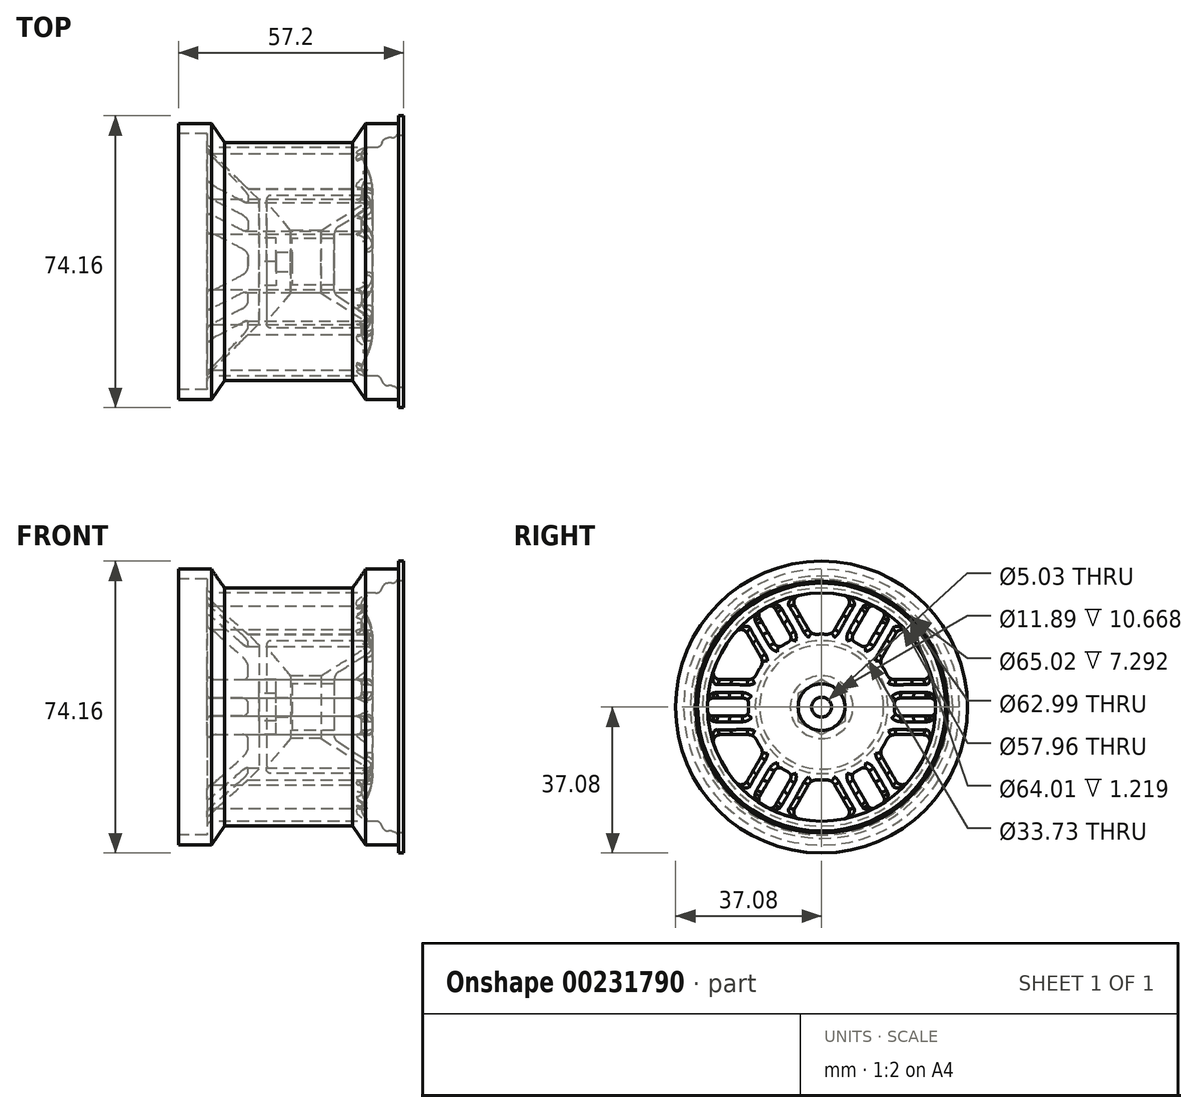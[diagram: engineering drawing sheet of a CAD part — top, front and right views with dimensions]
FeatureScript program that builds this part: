
annotation { "Feature Type Name" : "Feature", "Feature Type Description" : "" }
export const myFeature = defineFeature(function(context is Context, id is Id, definition is map)
    precondition{}
    {
        {
            var Q0;
            Q0=qCreatedBy(makeId("Front.planeOp"),FACE);
            var sketch = newSketch(context, id + "F0", { "sketchPlane" : qUnion([Q0])});
            skLineSegment(sketch, "E0.top", {"start": v(-20.52, 0) * mm, "end": v(36.68, 0) * mm});
            skLineSegment(sketch, "E0.left", {"start": v(-20.52, 35.05) * mm, "end": v(-20.52, 0) * mm});
            skLineSegment(sketch, "E0.right", {"start": v(36.68, 35.05) * mm, "end": v(36.68, 0) * mm});
            skLineSegment(sketch, "E1.top", {"start": v(36.68, 37.08) * mm, "end": v(35.46, 37.08) * mm});
            skLineSegment(sketch, "E1.left", {"start": v(36.68, 35.05) * mm, "end": v(36.68, 37.08) * mm});
            skLineSegment(sketch, "E1.right", {"start": v(35.46, 35.05) * mm, "end": v(35.46, 37.08) * mm});
            skLineSegment(sketch, "E2", {"start": v(35.46, 35.05) * mm, "end": v(36.68, 35.05) * mm, "construction": true});
            skPoint(sketch, "E3", {"position": v(0, 0) * mm});
            skLineSegment(sketch, "E4", {"start": v(-20.52, 35.05) * mm, "end": v(-12.14, 35.05) * mm});
            skLineSegment(sketch, "E5", {"start": v(-12.14, 35.05) * mm, "end": v(-8.76, 30.23) * mm});
            skLineSegment(sketch, "E6", {"start": v(-8.76, 30.23) * mm, "end": v(23.7, 30.23) * mm});
            skLineSegment(sketch, "E7", {"start": v(23.7, 30.23) * mm, "end": v(27.08, 35.05) * mm});
            skLineSegment(sketch, "E8", {"start": v(27.08, 35.05) * mm, "end": v(35.46, 35.05) * mm});
            skLineSegment(sketch, "E9", {"start": v(7.47, 30.23) * mm, "end": v(7.47, 0) * mm, "construction": true});
            skSolve(sketch);
        }
        {
            var Q0;
            Q0=makeQuery(id+"F0.imprint","IMPRINT",FACE,{"disambiguationData":[TD([[makeQuery(id+"F0.imprint","IMPRINT",EDGE,{"derivedFrom":sQuery(id+"F0.wireOp",EDGE,"E0.top")}),1.0]])]});
            var Q1;
            Q1=sQuery(id+"F0.wireOp",EDGE,"E0.top");
            revolve(context, id + "F1", {"entities" : qUnion([Q0]), "axis" : qUnion([Q1]), "revolveType" : RevolveType.FULL});
        }
        {
            var Q0;
            Q0=qCreatedBy(makeId("Right.planeOp"),FACE);
            cPlane(context, id + "F2", {"entities" : qUnion([Q0]), "cplaneType" : CPlaneType.OFFSET, "offset" : 13.2 * mm, "width" : 152.4 * mm, "height" : 152.4 * mm});
        }
        {
            var Q0;
            Q0=qCreatedBy(id+"F2.planeOp",FACE);
            var sketch = newSketch(context, id + "F3", { "sketchPlane" : qUnion([Q0])});
            skPoint(sketch, "E10", {"position": v(0, 0) * mm});
            skSolve(sketch);
        }
        {
            var Q0;
            Q0=sQuery(id+"F3.wireOp",VERTEX,"E10");
            var Q1;
            Q1=makeQuery(id+"F1.opRevolve","SWEPT_BODY",BODY,{"disambiguationData":[OSD([sQuery(id+"F0.wireOp",EDGE,"E0.top"),sQuery(id+"F0.wireOp",EDGE,"E0.left"),sQuery(id+"F0.wireOp",EDGE,"E0.right"),sQuery(id+"F0.wireOp",EDGE,"E1.top"),sQuery(id+"F0.wireOp",EDGE,"E1.left"),sQuery(id+"F0.wireOp",EDGE,"E1.right"),sQuery(id+"F0.wireOp",EDGE,"E4"),sQuery(id+"F0.wireOp",EDGE,"E5"),sQuery(id+"F0.wireOp",EDGE,"E6"),sQuery(id+"F0.wireOp",EDGE,"E7"),sQuery(id+"F0.wireOp",EDGE,"E8")])]});
            hole(context, id + "F4", {"style" : HoleStyle.SIMPLE, "endStyle" : HoleEndStyle.THROUGH, "oppositeDirection" : true, "holeDiameter" : 11.9 * mm, "locations" : qUnion([Q0]), "scope" : qUnion([Q1]), "isTappedThrough" : true});
        }
        {
            var Q0;
            Q0=sQuery(id+"F3.wireOp",VERTEX,"E10");
            var Q1;
            Q1=makeQuery(id+"F1.opRevolve","SWEPT_BODY",BODY,{"disambiguationData":[OSD([sQuery(id+"F0.wireOp",EDGE,"E0.top"),sQuery(id+"F0.wireOp",EDGE,"E0.left"),sQuery(id+"F0.wireOp",EDGE,"E0.right"),sQuery(id+"F0.wireOp",EDGE,"E1.top"),sQuery(id+"F0.wireOp",EDGE,"E1.left"),sQuery(id+"F0.wireOp",EDGE,"E1.right"),sQuery(id+"F0.wireOp",EDGE,"E4"),sQuery(id+"F0.wireOp",EDGE,"E5"),sQuery(id+"F0.wireOp",EDGE,"E6"),sQuery(id+"F0.wireOp",EDGE,"E7"),sQuery(id+"F0.wireOp",EDGE,"E8")])]});
            hole(context, id + "F5", {"style" : HoleStyle.C_BORE, "endStyle" : HoleEndStyle.THROUGH, "holeDiameter" : 5.03 * mm, "cBoreDiameter" : 11.9 * mm, "cBoreDepth" : 4.83 * mm, "locations" : qUnion([Q0]), "scope" : qUnion([Q1]), "isTappedThrough" : true});
        }
        {
            var Q0;
            Q0=qCreatedBy(makeId("Front.planeOp"),FACE);
            var sketch = newSketch(context, id + "F6", { "sketchPlane" : qUnion([Q0])});
            skLineSegment(sketch, "E11.bottom", {"start": v(0, 0) * mm, "end": v(-20.52, 0) * mm});
            skLineSegment(sketch, "E11.left", {"start": v(0, 0) * mm, "end": v(0, 15.75) * mm});
            skLineSegment(sketch, "E11.right", {"start": v(-20.52, 0) * mm, "end": v(-20.52, 32.51) * mm});
            skLineSegment(sketch, "E12", {"start": v(-20.52, 32.51) * mm, "end": v(-20.52, 35.05) * mm, "construction": true});
            skPoint(sketch, "E13.visualSharp", {"position": v(0, 15.75) * mm});
            skPoint(sketch, "E14.visualSharp", {"position": v(-20.52, 32.51) * mm});
            skLineSegment(sketch, "E15", {"start": v(-13.23, 28.98) * mm, "end": v(0, 15.75) * mm});
            skLineSegment(sketch, "E16", {"start": v(-20.52, 32.51) * mm, "end": v(-13.23, 32.51) * mm});
            skLineSegment(sketch, "E17", {"start": v(-13.23, 32.51) * mm, "end": v(-13.23, 28.98) * mm});
            skSolve(sketch);
        }
        {
            var Q0;
            Q0=qSketchRegion(id+"F6",true);
            var Q1;
            Q1=sQuery(id+"F6.wireOp",EDGE,"E11.bottom");
            revolve(context, id + "F7", {"operationType" : NewBodyOperationType.REMOVE, "entities" : qUnion([Q0]), "axis" : qUnion([Q1]), "revolveType" : RevolveType.FULL, "oppositeDirection" : true});
        }
        {
            var Q0;
            Q0=qCreatedBy(makeId("Right.planeOp"),FACE);
            var sketch = newSketch(context, id + "F8", { "sketchPlane" : qUnion([Q0])});
            skPoint(sketch, "E18", {"position": v(0.13, 0.17) * mm});
            skLineSegment(sketch, "E19", {"start": v(6.05, -3.5) * mm, "end": v(6.05, 3.5) * mm});
            skLineSegment(sketch, "E20", {"start": v(0, 0) * mm, "end": v(6.05, 0) * mm, "construction": true});
            skLineSegment(sketch, "E21.1.0", {"start": v(6.05, 3.5) * mm, "end": v(0, 6.98) * mm});
            skLineSegment(sketch, "E21.2.0", {"start": v(0, 6.98) * mm, "end": v(-6.05, 3.5) * mm});
            skLineSegment(sketch, "E21.3.0", {"start": v(-6.05, 3.5) * mm, "end": v(-6.05, -3.5) * mm});
            skLineSegment(sketch, "E21.4.0", {"start": v(-6.05, -3.5) * mm, "end": v(0, -6.98) * mm});
            skLineSegment(sketch, "E21.5.0", {"start": v(0, -6.98) * mm, "end": v(6.05, -3.5) * mm});
            skPoint(sketch, "E21.center", {"position": v(0, 0) * mm});
            skPoint(sketch, "E22.orphan", {"position": v(1.46, 7.82) * mm});
            skPoint(sketch, "E23.orphan", {"position": v(6.05, 5.17) * mm});
            skPoint(sketch, "E24.orphan", {"position": v(6.05, -5.17) * mm});
            skPoint(sketch, "E25.orphan", {"position": v(-1.46, 7.82) * mm});
            skPoint(sketch, "E26.orphan", {"position": v(7.5, 2.65) * mm});
            skPoint(sketch, "E27.orphan", {"position": v(7.5, -2.65) * mm});
            skPoint(sketch, "E28.orphan", {"position": v(1.46, -7.82) * mm});
            skPoint(sketch, "E29.orphan", {"position": v(-1.46, -7.82) * mm});
            skPoint(sketch, "E30.orphan", {"position": v(-6.05, -5.17) * mm});
            skPoint(sketch, "E31.orphan", {"position": v(-7.5, -2.65) * mm});
            skPoint(sketch, "E32.orphan", {"position": v(-7.5, 2.65) * mm});
            skPoint(sketch, "E33.orphan", {"position": v(-6.05, 5.17) * mm});
            skSolve(sketch);
        }
        {
            var Q0;
            Q0=qSketchRegion(id+"F8",true);
            extrude(context, id + "F9", {"entities" : qUnion([Q0]), "operationType" : NewBodyOperationType.REMOVE, "depth" : 4.32 * mm});
        }
        {
            var Q0;
            Q0=qCreatedBy(makeId("Front.planeOp"),FACE);
            var sketch = newSketch(context, id + "F10", { "sketchPlane" : qUnion([Q0])});
            skLineSegment(sketch, "E34", {"start": v(36.68, 32) * mm, "end": v(36.68, 37.08) * mm, "construction": true});
            skLineSegment(sketch, "E35", {"start": v(36.68, 32) * mm, "end": v(35.46, 32) * mm});
            skLineSegment(sketch, "E36", {"start": v(35.46, 32) * mm, "end": v(35.32, 33.33) * mm});
            skArc(sketch, "E37", {"start": v(35.32, 33.33) * mm, "mid": v(34.9, 32.04) * mm, "end": v(33.67, 31.5) * mm});
            skLineSegment(sketch, "E38", {"start": v(33.67, 31.5) * mm, "end": v(32.8, 31.5) * mm});
            skArc(sketch, "E39", {"start": v(32.8, 31.5) * mm, "mid": v(31.79, 31.14) * mm, "end": v(31.2, 30.24) * mm});
            skArc(sketch, "E40", {"start": v(29.59, 28.98) * mm, "mid": v(30.6, 29.33) * mm, "end": v(31.2, 30.24) * mm});
            skLineSegment(sketch, "E41", {"start": v(29.59, 28.98) * mm, "end": v(27.56, 28.98) * mm});
            skArc(sketch, "E42", {"start": v(27.56, 28.98) * mm, "mid": v(26.28, 28.29) * mm, "end": v(26.17, 26.83) * mm});
            skLineSegment(sketch, "E43", {"start": v(8.38, 5.94) * mm, "end": v(19.05, 5.94) * mm, "construction": true});
            skLineSegment(sketch, "E44", {"start": v(27.55, 23.75) * mm, "end": v(26.17, 26.83) * mm});
            skLineSegment(sketch, "E45", {"start": v(36.68, 32) * mm, "end": v(36.68, 0) * mm});
            skLineSegment(sketch, "E46", {"start": v(36.68, 0) * mm, "end": v(19.05, 0) * mm});
            skLineSegment(sketch, "E47", {"start": v(31.2, 30.24) * mm, "end": v(30.65, 28.06) * mm, "construction": true});
            skLineSegment(sketch, "E48", {"start": v(19.05, 5.94) * mm, "end": v(19.05, 6.86) * mm});
            skPoint(sketch, "E49.visualSharp", {"position": v(19.05, 6.86) * mm});
            skArc(sketch, "E49.filletArc", {"start": v(28.77, 18.03) * mm, "mid": v(28.46, 20.96) * mm, "end": v(27.55, 23.75) * mm});
            skLineSegment(sketch, "E50", {"start": v(28.77, 18.03) * mm, "end": v(28.77, 15.75) * mm});
            skLineSegment(sketch, "E51", {"start": v(20.24, 9.01) * mm, "end": v(27.58, 13.6) * mm});
            skArc(sketch, "E52", {"start": v(28.77, 15.75) * mm, "mid": v(28.45, 14.52) * mm, "end": v(27.58, 13.6) * mm});
            skArc(sketch, "E53", {"start": v(20.24, 9.01) * mm, "mid": v(19.37, 8.09) * mm, "end": v(19.05, 6.86) * mm});
            skLineSegment(sketch, "E54", {"start": v(19.05, 5.94) * mm, "end": v(19.05, 0) * mm});
            skSolve(sketch);
        }
        {
            var Q0;
            Q0=qSketchRegion(id+"F10",true);
            var Q1;
            Q1=sQuery(id+"F10.wireOp",EDGE,"E46");
            revolve(context, id + "F11", {"operationType" : NewBodyOperationType.REMOVE, "entities" : qUnion([Q0]), "axis" : qUnion([Q1]), "revolveType" : RevolveType.FULL, "oppositeDirection" : true});
        }
        {
            var Q0;
            Q0=makeQuery(id+"F1.opRevolve","SWEPT_FACE",FACE,{"disambiguationData":[OSD([sQuery(id+"F0.wireOp",EDGE,"E0.right"),sQuery(id+"F0.wireOp",EDGE,"E1.left")])]});
            cPlane(context, id + "F12", {"entities" : qUnion([Q0]), "cplaneType" : CPlaneType.OFFSET, "offset" : 0 * mm, "width" : 152.4 * mm, "height" : 152.4 * mm});
        }
        {
            var Q0;
            Q0=qCreatedBy(id+"F12.planeOp",FACE);
            var sketch = newSketch(context, id + "F13", { "sketchPlane" : qUnion([Q0])});
            skLineSegment(sketch, "E55", {"start": v(6.83, 25.8) * mm, "end": v(3.28, 19.64) * mm});
            skLineSegment(sketch, "E56", {"start": v(0, 28.98) * mm, "end": v(0, 18.54) * mm, "construction": true});
            skArc(sketch, "E57", {"start": v(5.63, 28.43) * mm, "mid": v(2.83, 28.84) * mm, "end": v(0, 28.98) * mm});
            skArc(sketch, "E58", {"start": v(5.63, 28.43) * mm, "mid": v(6.9, 27.42) * mm, "end": v(6.83, 25.8) * mm});
            skLineSegment(sketch, "E59", {"start": v(0, 0) * mm, "end": v(0, 13.97) * mm, "construction": true});
            skArc(sketch, "E60", {"start": v(0, 18.54) * mm, "mid": v(0.58, 18.53) * mm, "end": v(1.15, 18.5) * mm});
            skArc(sketch, "E61.filletArc", {"start": v(1.15, 18.5) * mm, "mid": v(2.38, 18.77) * mm, "end": v(3.28, 19.64) * mm});
            skArc(sketch, "E62.MirrorCS", {"start": v(0, 18.54) * mm, "mid": v(-0.58, 18.53) * mm, "end": v(-1.15, 18.5) * mm});
            skArc(sketch, "E63.MirrorCS", {"start": v(-1.15, 18.5) * mm, "mid": v(-2.38, 18.77) * mm, "end": v(-3.28, 19.64) * mm});
            skLineSegment(sketch, "E64.MirrorCS", {"start": v(-6.83, 25.8) * mm, "end": v(-3.28, 19.64) * mm});
            skArc(sketch, "E65.MirrorCS", {"start": v(-5.63, 28.43) * mm, "mid": v(-6.9, 27.42) * mm, "end": v(-6.83, 25.8) * mm});
            skArc(sketch, "E66.MirrorCS", {"start": v(-5.63, 28.43) * mm, "mid": v(-2.83, 28.84) * mm, "end": v(0, 28.98) * mm});
            skLineSegment(sketch, "E67", {"start": v(0, 13.97) * mm, "end": v(3.28, 19.64) * mm, "construction": true});
            skSolve(sketch);
        }
        {
            var Q0;
            Q0 = qSketchRegion(id + "F13", true);
            extrude(context, id + "F14", {"entities" : qUnion([Q0]), "endBound" : BoundingType.THROUGH_ALL, "oppositeDirection" : true, "depth" : 71.11 * mm});
        }
        {
            var Q0;
            Q0=makeQuery(id+"F14.opExtrude","SWEPT_BODY",BODY,{"disambiguationData":[OSD([sQuery(id+"F13.wireOp",EDGE,"E55"),sQuery(id+"F13.wireOp",EDGE,"E57"),sQuery(id+"F13.wireOp",EDGE,"E58"),sQuery(id+"F13.wireOp",EDGE,"E60"),sQuery(id+"F13.wireOp",EDGE,"E61.filletArc"),sQuery(id+"F13.wireOp",EDGE,"E62.MirrorCS"),sQuery(id+"F13.wireOp",EDGE,"E63.MirrorCS"),sQuery(id+"F13.wireOp",EDGE,"E64.MirrorCS"),sQuery(id+"F13.wireOp",EDGE,"E65.MirrorCS"),sQuery(id+"F13.wireOp",EDGE,"E66.MirrorCS")])]});
            var Q1;
            Q1=sQuery(id+"F0.wireOp",EDGE,"E0.top");
            circularPattern(context, id + "F15", {"operationType" : NewBodyOperationType.REMOVE, "entities" : qUnion([Q0]), "axis" : qUnion([Q1]), "angle" : 360 * degree, "instanceCount" : 6, "equalSpace" : true});
        }
        {
            var Q0;
            Q0=makeQuery(id+"F15.boolean.opBoolean","SPLIT",FACE,{"disambiguationData":[TD([makeQuery(id+"F15.opPattern","COPY",FACE,{"derivedFrom":makeQuery(id+"F14.opExtrude","SWEPT_FACE",FACE,{"disambiguationData":[OSD([sQuery(id+"F13.wireOp",EDGE,"E55")])]}),"instanceName":"2"})])],"derivedFrom":makeQuery(id+"F11.boolean.opBoolean","COPY",FACE,{"derivedFrom":makeQuery(id+"F11.opRevolve","SWEPT_FACE",FACE,{"disambiguationData":[OSD([sQuery(id+"F10.wireOp",EDGE,"E44")])]})})});
            var Q1;
            Q1=makeQuery(id+"F15.boolean.opBoolean","SPLIT",FACE,{"disambiguationData":[TD([makeQuery(id+"F15.opPattern","COPY",FACE,{"derivedFrom":makeQuery(id+"F14.opExtrude","SWEPT_FACE",FACE,{"disambiguationData":[OSD([sQuery(id+"F13.wireOp",EDGE,"E55")])]}),"instanceName":"2"})])],"derivedFrom":makeQuery(id+"F11.boolean.opBoolean","COPY",FACE,{"derivedFrom":makeQuery(id+"F11.opRevolve","SWEPT_FACE",FACE,{"disambiguationData":[OSD([sQuery(id+"F10.wireOp",EDGE,"E49.filletArc")])]})})});
            var Q2;
            Q2=makeQuery(id+"F15.boolean.opBoolean","SPLIT",FACE,{"disambiguationData":[TD([makeQuery(id+"F15.opPattern","COPY",FACE,{"derivedFrom":makeQuery(id+"F14.opExtrude","SWEPT_FACE",FACE,{"disambiguationData":[OSD([sQuery(id+"F13.wireOp",EDGE,"E58")])]}),"instanceName":"2"})])],"derivedFrom":makeQuery(id+"F11.boolean.opBoolean","COPY",FACE,{"derivedFrom":makeQuery(id+"F11.opRevolve","SWEPT_FACE",FACE,{"disambiguationData":[OSD([sQuery(id+"F10.wireOp",EDGE,"E42")])]})})});
            var Q3;
            Q3=makeQuery(id+"F15.boolean.opBoolean","SPLIT",FACE,{"disambiguationData":[TD([makeQuery(id+"F15.opPattern","COPY",FACE,{"derivedFrom":makeQuery(id+"F14.opExtrude","SWEPT_FACE",FACE,{"disambiguationData":[OSD([sQuery(id+"F13.wireOp",EDGE,"E55")])]}),"instanceName":"1"})])],"derivedFrom":makeQuery(id+"F11.boolean.opBoolean","COPY",FACE,{"derivedFrom":makeQuery(id+"F11.opRevolve","SWEPT_FACE",FACE,{"disambiguationData":[OSD([sQuery(id+"F10.wireOp",EDGE,"E44")])]})})});
            var Q4;
            Q4=makeQuery(id+"F15.boolean.opBoolean","SPLIT",FACE,{"disambiguationData":[TD([makeQuery(id+"F15.opPattern","COPY",FACE,{"derivedFrom":makeQuery(id+"F14.opExtrude","SWEPT_FACE",FACE,{"disambiguationData":[OSD([sQuery(id+"F13.wireOp",EDGE,"E55")])]}),"instanceName":"1"})])],"derivedFrom":makeQuery(id+"F11.boolean.opBoolean","COPY",FACE,{"derivedFrom":makeQuery(id+"F11.opRevolve","SWEPT_FACE",FACE,{"disambiguationData":[OSD([sQuery(id+"F10.wireOp",EDGE,"E49.filletArc")])]})})});
            var Q5;
            Q5=makeQuery(id+"F15.boolean.opBoolean","SPLIT",FACE,{"disambiguationData":[TD([makeQuery(id+"F15.opPattern","COPY",FACE,{"derivedFrom":makeQuery(id+"F14.opExtrude","SWEPT_FACE",FACE,{"disambiguationData":[OSD([sQuery(id+"F13.wireOp",EDGE,"E58")])]}),"instanceName":"1"})])],"derivedFrom":makeQuery(id+"F11.boolean.opBoolean","COPY",FACE,{"derivedFrom":makeQuery(id+"F11.opRevolve","SWEPT_FACE",FACE,{"disambiguationData":[OSD([sQuery(id+"F10.wireOp",EDGE,"E42")])]})})});
            var Q6;
            Q6=makeQuery(id+"F15.boolean.opBoolean","SPLIT",FACE,{"disambiguationData":[TD([makeQuery(id+"F15.opPattern","COPY",FACE,{"derivedFrom":makeQuery(id+"F14.opExtrude","SWEPT_FACE",FACE,{"disambiguationData":[OSD([sQuery(id+"F13.wireOp",EDGE,"E55")])]}),"instanceName":"3"})])],"derivedFrom":makeQuery(id+"F11.boolean.opBoolean","COPY",FACE,{"derivedFrom":makeQuery(id+"F11.opRevolve","SWEPT_FACE",FACE,{"disambiguationData":[OSD([sQuery(id+"F10.wireOp",EDGE,"E44")])]})})});
            var Q7;
            Q7=makeQuery(id+"F11.boolean.opBoolean","COPY",FACE,{"derivedFrom":makeQuery(id+"F11.opRevolve","SWEPT_FACE",FACE,{"disambiguationData":[OSD([sQuery(id+"F10.wireOp",EDGE,"E50")])]})});
            var Q8;
            Q8=makeQuery(id+"F15.boolean.opBoolean","SPLIT",FACE,{"disambiguationData":[TD([makeQuery(id+"F15.opPattern","COPY",FACE,{"derivedFrom":makeQuery(id+"F14.opExtrude","SWEPT_FACE",FACE,{"disambiguationData":[OSD([sQuery(id+"F13.wireOp",EDGE,"E55")])]}),"instanceName":"3"})])],"derivedFrom":makeQuery(id+"F11.boolean.opBoolean","COPY",FACE,{"derivedFrom":makeQuery(id+"F11.opRevolve","SWEPT_FACE",FACE,{"disambiguationData":[OSD([sQuery(id+"F10.wireOp",EDGE,"E49.filletArc")])]})})});
            var Q9;
            Q9=makeQuery(id+"F15.boolean.opBoolean","SPLIT",FACE,{"disambiguationData":[TD([makeQuery(id+"F15.opPattern","COPY",FACE,{"derivedFrom":makeQuery(id+"F14.opExtrude","SWEPT_FACE",FACE,{"disambiguationData":[OSD([sQuery(id+"F13.wireOp",EDGE,"E58")])]}),"instanceName":"3"})])],"derivedFrom":makeQuery(id+"F11.boolean.opBoolean","COPY",FACE,{"derivedFrom":makeQuery(id+"F11.opRevolve","SWEPT_FACE",FACE,{"disambiguationData":[OSD([sQuery(id+"F10.wireOp",EDGE,"E42")])]})})});
            var Q10;
            Q10=makeQuery(id+"F15.boolean.opBoolean","SPLIT",FACE,{"disambiguationData":[TD([makeQuery(id+"F15.opPattern","COPY",FACE,{"derivedFrom":makeQuery(id+"F14.opExtrude","SWEPT_FACE",FACE,{"disambiguationData":[OSD([sQuery(id+"F13.wireOp",EDGE,"E55")])]}),"instanceName":"4"})])],"derivedFrom":makeQuery(id+"F11.boolean.opBoolean","COPY",FACE,{"derivedFrom":makeQuery(id+"F11.opRevolve","SWEPT_FACE",FACE,{"disambiguationData":[OSD([sQuery(id+"F10.wireOp",EDGE,"E49.filletArc")])]})})});
            var Q11;
            Q11=makeQuery(id+"F15.boolean.opBoolean","SPLIT",FACE,{"disambiguationData":[TD([makeQuery(id+"F15.opPattern","COPY",FACE,{"derivedFrom":makeQuery(id+"F14.opExtrude","SWEPT_FACE",FACE,{"disambiguationData":[OSD([sQuery(id+"F13.wireOp",EDGE,"E55")])]}),"instanceName":"4"})])],"derivedFrom":makeQuery(id+"F11.boolean.opBoolean","COPY",FACE,{"derivedFrom":makeQuery(id+"F11.opRevolve","SWEPT_FACE",FACE,{"disambiguationData":[OSD([sQuery(id+"F10.wireOp",EDGE,"E44")])]})})});
            var Q12;
            Q12=makeQuery(id+"F15.boolean.opBoolean","SPLIT",FACE,{"disambiguationData":[TD([makeQuery(id+"F15.opPattern","COPY",FACE,{"derivedFrom":makeQuery(id+"F14.opExtrude","SWEPT_FACE",FACE,{"disambiguationData":[OSD([sQuery(id+"F13.wireOp",EDGE,"E58")])]}),"instanceName":"4"})])],"derivedFrom":makeQuery(id+"F11.boolean.opBoolean","COPY",FACE,{"derivedFrom":makeQuery(id+"F11.opRevolve","SWEPT_FACE",FACE,{"disambiguationData":[OSD([sQuery(id+"F10.wireOp",EDGE,"E42")])]})})});
            var Q13;
            Q13=makeQuery(id+"F15.boolean.opBoolean","SPLIT",FACE,{"disambiguationData":[TD([makeQuery(id+"F14.opExtrude","SWEPT_FACE",FACE,{"disambiguationData":[OSD([sQuery(id+"F13.wireOp",EDGE,"E63.MirrorCS")])]})])],"derivedFrom":makeQuery(id+"F11.boolean.opBoolean","COPY",FACE,{"derivedFrom":makeQuery(id+"F11.opRevolve","SWEPT_FACE",FACE,{"disambiguationData":[OSD([sQuery(id+"F10.wireOp",EDGE,"E49.filletArc")])]})})});
            var Q14;
            Q14=makeQuery(id+"F15.boolean.opBoolean","SPLIT",FACE,{"disambiguationData":[TD([makeQuery(id+"F14.opExtrude","SWEPT_FACE",FACE,{"disambiguationData":[OSD([sQuery(id+"F13.wireOp",EDGE,"E64.MirrorCS")])]})])],"derivedFrom":makeQuery(id+"F11.boolean.opBoolean","COPY",FACE,{"derivedFrom":makeQuery(id+"F11.opRevolve","SWEPT_FACE",FACE,{"disambiguationData":[OSD([sQuery(id+"F10.wireOp",EDGE,"E44")])]})})});
            var Q15;
            Q15=makeQuery(id+"F15.boolean.opBoolean","SPLIT",FACE,{"disambiguationData":[TD([makeQuery(id+"F14.opExtrude","SWEPT_FACE",FACE,{"disambiguationData":[OSD([sQuery(id+"F13.wireOp",EDGE,"E65.MirrorCS")])]})])],"derivedFrom":makeQuery(id+"F11.boolean.opBoolean","COPY",FACE,{"derivedFrom":makeQuery(id+"F11.opRevolve","SWEPT_FACE",FACE,{"disambiguationData":[OSD([sQuery(id+"F10.wireOp",EDGE,"E42")])]})})});
            var Q16;
            Q16=makeQuery(id+"F15.boolean.opBoolean","SPLIT",FACE,{"disambiguationData":[TD([makeQuery(id+"F14.opExtrude","SWEPT_FACE",FACE,{"disambiguationData":[OSD([sQuery(id+"F13.wireOp",EDGE,"E55")])]})])],"derivedFrom":makeQuery(id+"F11.boolean.opBoolean","COPY",FACE,{"derivedFrom":makeQuery(id+"F11.opRevolve","SWEPT_FACE",FACE,{"disambiguationData":[OSD([sQuery(id+"F10.wireOp",EDGE,"E44")])]})})});
            var Q17;
            Q17=makeQuery(id+"F15.boolean.opBoolean","SPLIT",FACE,{"disambiguationData":[TD([makeQuery(id+"F14.opExtrude","SWEPT_FACE",FACE,{"disambiguationData":[OSD([sQuery(id+"F13.wireOp",EDGE,"E55")])]})])],"derivedFrom":makeQuery(id+"F11.boolean.opBoolean","COPY",FACE,{"derivedFrom":makeQuery(id+"F11.opRevolve","SWEPT_FACE",FACE,{"disambiguationData":[OSD([sQuery(id+"F10.wireOp",EDGE,"E49.filletArc")])]})})});
            var Q18;
            Q18=makeQuery(id+"F15.boolean.opBoolean","SPLIT",FACE,{"disambiguationData":[TD([makeQuery(id+"F14.opExtrude","SWEPT_FACE",FACE,{"disambiguationData":[OSD([sQuery(id+"F13.wireOp",EDGE,"E58")])]})])],"derivedFrom":makeQuery(id+"F11.boolean.opBoolean","COPY",FACE,{"derivedFrom":makeQuery(id+"F11.opRevolve","SWEPT_FACE",FACE,{"disambiguationData":[OSD([sQuery(id+"F10.wireOp",EDGE,"E42")])]})})});
            var Q19;
            Q19=makeQuery(id+"F15.boolean.opBoolean","SPLIT",FACE,{"disambiguationData":[TD([makeQuery(id+"F15.opPattern","COPY",FACE,{"derivedFrom":makeQuery(id+"F14.opExtrude","SWEPT_FACE",FACE,{"disambiguationData":[OSD([sQuery(id+"F13.wireOp",EDGE,"E64.MirrorCS")])]}),"instanceName":"4"})])],"derivedFrom":makeQuery(id+"F11.boolean.opBoolean","COPY",FACE,{"derivedFrom":makeQuery(id+"F11.opRevolve","SWEPT_FACE",FACE,{"disambiguationData":[OSD([sQuery(id+"F10.wireOp",EDGE,"E44")])]})})});
            var Q20;
            Q20=makeQuery(id+"F15.boolean.opBoolean","SPLIT",FACE,{"disambiguationData":[TD([makeQuery(id+"F15.opPattern","COPY",FACE,{"derivedFrom":makeQuery(id+"F14.opExtrude","SWEPT_FACE",FACE,{"disambiguationData":[OSD([sQuery(id+"F13.wireOp",EDGE,"E65.MirrorCS")])]}),"instanceName":"4"})])],"derivedFrom":makeQuery(id+"F11.boolean.opBoolean","COPY",FACE,{"derivedFrom":makeQuery(id+"F11.opRevolve","SWEPT_FACE",FACE,{"disambiguationData":[OSD([sQuery(id+"F10.wireOp",EDGE,"E42")])]})})});
            fillet(context, id + "F16", {"entities" : qUnion([Q0, Q1, Q2, Q3, Q4, Q5, Q6, Q7, Q8, Q9, Q10, Q11, Q12, Q13, Q14, Q15, Q16, Q17, Q18, Q19, Q20]), "radius" : 1.37 * mm, "allowEdgeOverflow" : false});
        }
        {
            var Q0;
            Q0=qCreatedBy(id+"F12.planeOp",FACE);
            var sketch = newSketch(context, id + "F17", { "sketchPlane" : qUnion([Q0])});
            skPoint(sketch, "E68", {"position": v(0, 0) * mm});
            skLineSegment(sketch, "E69", {"start": v(0, 0) * mm, "end": v(16.02, 27.74) * mm, "construction": true});
            skLineSegment(sketch, "E70", {"start": v(11.93, 16.08) * mm, "end": v(15.78, 22.75) * mm});
            skArc(sketch, "E71", {"start": v(9.27, 16.06) * mm, "mid": v(9.64, 15.84) * mm, "end": v(10, 15.62) * mm});
            skArc(sketch, "E72", {"start": v(14.5, 25.1) * mm, "mid": v(14.9, 24.86) * mm, "end": v(15.31, 24.6) * mm});
            skPoint(sketch, "E73.visualSharp", {"position": v(16.43, 23.88) * mm});
            skArc(sketch, "E73.filletArc", {"start": v(15.78, 22.75) * mm, "mid": v(15.92, 23.77) * mm, "end": v(15.31, 24.6) * mm});
            skPoint(sketch, "E74.visualSharp", {"position": v(11.18, 14.8) * mm});
            skArc(sketch, "E74.filletArc", {"start": v(10, 15.62) * mm, "mid": v(11.06, 15.44) * mm, "end": v(11.93, 16.08) * mm});
            skArc(sketch, "E75.MirrorCS", {"start": v(9.27, 16.06) * mm, "mid": v(8.9, 16.27) * mm, "end": v(8.52, 16.47) * mm});
            skArc(sketch, "E76.MirrorCS", {"start": v(8.52, 16.47) * mm, "mid": v(7.84, 17.3) * mm, "end": v(7.97, 18.37) * mm});
            skLineSegment(sketch, "E77.MirrorCS", {"start": v(7.97, 18.37) * mm, "end": v(11.82, 25.04) * mm});
            skArc(sketch, "E78.MirrorCS", {"start": v(11.82, 25.04) * mm, "mid": v(12.63, 25.67) * mm, "end": v(13.65, 25.56) * mm});
            skArc(sketch, "E79.MirrorCS", {"start": v(14.5, 25.1) * mm, "mid": v(14.07, 25.34) * mm, "end": v(13.65, 25.56) * mm});
            skSolve(sketch);
        }
        {
            var Q0;
            Q0 = qSketchRegion(id + "F17", true);
            extrude(context, id + "F18", {"entities" : qUnion([Q0]), "endBound" : BoundingType.THROUGH_ALL, "oppositeDirection" : true, "depth" : 25.4 * mm});
        }
        {
            var Q0;
            Q0=makeQuery(id+"F18.opExtrude","SWEPT_BODY",BODY,{"disambiguationData":[OSD([sQuery(id+"F17.wireOp",EDGE,"E70"),sQuery(id+"F17.wireOp",EDGE,"E71"),sQuery(id+"F17.wireOp",EDGE,"E72"),sQuery(id+"F17.wireOp",EDGE,"E73.filletArc"),sQuery(id+"F17.wireOp",EDGE,"E74.filletArc"),sQuery(id+"F17.wireOp",EDGE,"E75.MirrorCS"),sQuery(id+"F17.wireOp",EDGE,"E76.MirrorCS"),sQuery(id+"F17.wireOp",EDGE,"E77.MirrorCS"),sQuery(id+"F17.wireOp",EDGE,"E78.MirrorCS"),sQuery(id+"F17.wireOp",EDGE,"E79.MirrorCS")])]});
            var Q1;
            Q1=sQuery(id+"F0.wireOp",EDGE,"E0.top");
            circularPattern(context, id + "F19", {"operationType" : NewBodyOperationType.REMOVE, "entities" : qUnion([Q0]), "axis" : qUnion([Q1]), "angle" : 360 * degree, "instanceCount" : 6, "equalSpace" : true});
        }
        {
            var Q0;
            {var subQ2=sQuery(id+"F10.wireOp",EDGE,"E49.filletArc");var subQ3=makeQuery(id+"F11.boolean.opBoolean","COPY",FACE,{"derivedFrom":makeQuery(id+"F11.opRevolve","SWEPT_FACE",FACE,{"disambiguationData":[OSD([subQ2])]})});var subQ8=sQuery(id+"F13.wireOp",EDGE,"E55");var subQ9=makeQuery(id+"F15.opPattern","COPY",FACE,{"derivedFrom":makeQuery(id+"F14.opExtrude","SWEPT_FACE",FACE,{"disambiguationData":[OSD([subQ8])]}),"instanceName":"3"});Q0=makeQuery(id+"F19.boolean.opBoolean","SPLIT",FACE,{"disambiguationData":[TD([makeQuery(id+"F19.opPattern","COPY",FACE,{"derivedFrom":makeQuery(id+"F18.opExtrude","SWEPT_FACE",FACE,{"disambiguationData":[OSD([sQuery(id+"F17.wireOp",EDGE,"E76.MirrorCS")])]}),"instanceName":"3"})])],"derivedFrom":makeQuery(id+"F15.boolean.opBoolean","SPLIT",FACE,{"disambiguationData":[TD([subQ9])],"derivedFrom":subQ3})});}
            var Q1;
            {var subQ0=sQuery(id+"F13.wireOp",EDGE,"E58");var subQ1=makeQuery(id+"F15.opPattern","COPY",FACE,{"derivedFrom":makeQuery(id+"F14.opExtrude","SWEPT_FACE",FACE,{"disambiguationData":[OSD([subQ0])]}),"instanceName":"3"});var subQ2=sQuery(id+"F10.wireOp",EDGE,"E42");var subQ3=makeQuery(id+"F11.boolean.opBoolean","COPY",FACE,{"derivedFrom":makeQuery(id+"F11.opRevolve","SWEPT_FACE",FACE,{"disambiguationData":[OSD([subQ2])]})});Q1=makeQuery(id+"F19.boolean.opBoolean","SPLIT",FACE,{"disambiguationData":[TD([makeQuery(id+"F19.opPattern","COPY",FACE,{"derivedFrom":makeQuery(id+"F18.opExtrude","SWEPT_FACE",FACE,{"disambiguationData":[OSD([sQuery(id+"F17.wireOp",EDGE,"E77.MirrorCS")])]}),"instanceName":"3"})])],"derivedFrom":makeQuery(id+"F15.boolean.opBoolean","SPLIT",FACE,{"disambiguationData":[TD([subQ1])],"derivedFrom":subQ3})});}
            var Q2;
            {var subQ2=sQuery(id+"F10.wireOp",EDGE,"E49.filletArc");var subQ3=makeQuery(id+"F11.boolean.opBoolean","COPY",FACE,{"derivedFrom":makeQuery(id+"F11.opRevolve","SWEPT_FACE",FACE,{"disambiguationData":[OSD([subQ2])]})});Q2=makeQuery(id+"F19.boolean.opBoolean","SPLIT",FACE,{"disambiguationData":[TD([makeQuery(id+"F19.opPattern","COPY",FACE,{"derivedFrom":makeQuery(id+"F18.opExtrude","SWEPT_FACE",FACE,{"disambiguationData":[OSD([sQuery(id+"F17.wireOp",EDGE,"E74.filletArc")])]}),"instanceName":"3"})])],"derivedFrom":makeQuery(id+"F15.boolean.opBoolean","SPLIT",FACE,{"disambiguationData":[TD([makeQuery(id+"F15.opPattern","COPY",FACE,{"derivedFrom":makeQuery(id+"F14.opExtrude","SWEPT_FACE",FACE,{"disambiguationData":[OSD([sQuery(id+"F13.wireOp",EDGE,"E55")])]}),"instanceName":"3"})])],"derivedFrom":subQ3})});}
            var Q3;
            {var subQ2=sQuery(id+"F10.wireOp",EDGE,"E44");var subQ3=makeQuery(id+"F11.boolean.opBoolean","COPY",FACE,{"derivedFrom":makeQuery(id+"F11.opRevolve","SWEPT_FACE",FACE,{"disambiguationData":[OSD([subQ2])]})});Q3=makeQuery(id+"F19.boolean.opBoolean","SPLIT",FACE,{"disambiguationData":[TD([makeQuery(id+"F19.opPattern","COPY",FACE,{"derivedFrom":makeQuery(id+"F18.opExtrude","SWEPT_FACE",FACE,{"disambiguationData":[OSD([sQuery(id+"F17.wireOp",EDGE,"E70")])]}),"instanceName":"3"})])],"derivedFrom":makeQuery(id+"F15.boolean.opBoolean","SPLIT",FACE,{"disambiguationData":[TD([makeQuery(id+"F15.opPattern","COPY",FACE,{"derivedFrom":makeQuery(id+"F14.opExtrude","SWEPT_FACE",FACE,{"disambiguationData":[OSD([sQuery(id+"F13.wireOp",EDGE,"E55")])]}),"instanceName":"3"})])],"derivedFrom":subQ3})});}
            var Q4;
            {var subQ2=sQuery(id+"F10.wireOp",EDGE,"E42");var subQ3=makeQuery(id+"F11.boolean.opBoolean","COPY",FACE,{"derivedFrom":makeQuery(id+"F11.opRevolve","SWEPT_FACE",FACE,{"disambiguationData":[OSD([subQ2])]})});Q4=makeQuery(id+"F19.boolean.opBoolean","SPLIT",FACE,{"disambiguationData":[TD([makeQuery(id+"F19.opPattern","COPY",FACE,{"derivedFrom":makeQuery(id+"F18.opExtrude","SWEPT_FACE",FACE,{"disambiguationData":[OSD([sQuery(id+"F17.wireOp",EDGE,"E70")])]}),"instanceName":"3"})])],"derivedFrom":makeQuery(id+"F15.boolean.opBoolean","SPLIT",FACE,{"disambiguationData":[TD([makeQuery(id+"F15.opPattern","COPY",FACE,{"derivedFrom":makeQuery(id+"F14.opExtrude","SWEPT_FACE",FACE,{"disambiguationData":[OSD([sQuery(id+"F13.wireOp",EDGE,"E58")])]}),"instanceName":"3"})])],"derivedFrom":subQ3})});}
            var Q5;
            {var subQ2=sQuery(id+"F10.wireOp",EDGE,"E42");var subQ3=makeQuery(id+"F11.boolean.opBoolean","COPY",FACE,{"derivedFrom":makeQuery(id+"F11.opRevolve","SWEPT_FACE",FACE,{"disambiguationData":[OSD([subQ2])]})});Q5=makeQuery(id+"F19.boolean.opBoolean","SPLIT",FACE,{"disambiguationData":[TD([makeQuery(id+"F19.opPattern","COPY",FACE,{"derivedFrom":makeQuery(id+"F18.opExtrude","SWEPT_FACE",FACE,{"disambiguationData":[OSD([sQuery(id+"F17.wireOp",EDGE,"E77.MirrorCS")])]}),"instanceName":"1"})])],"derivedFrom":makeQuery(id+"F15.boolean.opBoolean","SPLIT",FACE,{"disambiguationData":[TD([makeQuery(id+"F14.opExtrude","SWEPT_FACE",FACE,{"disambiguationData":[OSD([sQuery(id+"F13.wireOp",EDGE,"E65.MirrorCS")])]})])],"derivedFrom":subQ3})});}
            var Q6;
            {var subQ4=sQuery(id+"F10.wireOp",EDGE,"E49.filletArc");var subQ5=makeQuery(id+"F11.boolean.opBoolean","COPY",FACE,{"derivedFrom":makeQuery(id+"F11.opRevolve","SWEPT_FACE",FACE,{"disambiguationData":[OSD([subQ4])]})});Q6=makeQuery(id+"F19.boolean.opBoolean","SPLIT",FACE,{"disambiguationData":[TD([makeQuery(id+"F19.opPattern","COPY",FACE,{"derivedFrom":makeQuery(id+"F18.opExtrude","SWEPT_FACE",FACE,{"disambiguationData":[OSD([sQuery(id+"F17.wireOp",EDGE,"E76.MirrorCS")])]}),"instanceName":"1"})])],"derivedFrom":makeQuery(id+"F15.boolean.opBoolean","SPLIT",FACE,{"disambiguationData":[TD([makeQuery(id+"F14.opExtrude","SWEPT_FACE",FACE,{"disambiguationData":[OSD([sQuery(id+"F13.wireOp",EDGE,"E63.MirrorCS")])]})])],"derivedFrom":subQ5})});}
            var Q7;
            {var subQ0=sQuery(id+"F13.wireOp",EDGE,"E63.MirrorCS");var subQ1=makeQuery(id+"F14.opExtrude","SWEPT_FACE",FACE,{"disambiguationData":[OSD([subQ0])]});var subQ2=sQuery(id+"F10.wireOp",EDGE,"E49.filletArc");var subQ3=makeQuery(id+"F11.boolean.opBoolean","COPY",FACE,{"derivedFrom":makeQuery(id+"F11.opRevolve","SWEPT_FACE",FACE,{"disambiguationData":[OSD([subQ2])]})});Q7=makeQuery(id+"F19.boolean.opBoolean","SPLIT",FACE,{"disambiguationData":[TD([makeQuery(id+"F19.opPattern","COPY",FACE,{"derivedFrom":makeQuery(id+"F18.opExtrude","SWEPT_FACE",FACE,{"disambiguationData":[OSD([sQuery(id+"F17.wireOp",EDGE,"E74.filletArc")])]}),"instanceName":"1"})])],"derivedFrom":makeQuery(id+"F15.boolean.opBoolean","SPLIT",FACE,{"disambiguationData":[TD([subQ1])],"derivedFrom":subQ3})});}
            var Q8;
            {var subQ0=sQuery(id+"F13.wireOp",EDGE,"E64.MirrorCS");var subQ1=makeQuery(id+"F14.opExtrude","SWEPT_FACE",FACE,{"disambiguationData":[OSD([subQ0])]});var subQ2=sQuery(id+"F10.wireOp",EDGE,"E44");var subQ3=makeQuery(id+"F11.boolean.opBoolean","COPY",FACE,{"derivedFrom":makeQuery(id+"F11.opRevolve","SWEPT_FACE",FACE,{"disambiguationData":[OSD([subQ2])]})});Q8=makeQuery(id+"F19.boolean.opBoolean","SPLIT",FACE,{"disambiguationData":[TD([makeQuery(id+"F19.opPattern","COPY",FACE,{"derivedFrom":makeQuery(id+"F18.opExtrude","SWEPT_FACE",FACE,{"disambiguationData":[OSD([sQuery(id+"F17.wireOp",EDGE,"E70")])]}),"instanceName":"1"})])],"derivedFrom":makeQuery(id+"F15.boolean.opBoolean","SPLIT",FACE,{"disambiguationData":[TD([subQ1])],"derivedFrom":subQ3})});}
            var Q9;
            {var subQ0=sQuery(id+"F13.wireOp",EDGE,"E65.MirrorCS");var subQ1=makeQuery(id+"F14.opExtrude","SWEPT_FACE",FACE,{"disambiguationData":[OSD([subQ0])]});var subQ2=sQuery(id+"F10.wireOp",EDGE,"E42");var subQ3=makeQuery(id+"F11.boolean.opBoolean","COPY",FACE,{"derivedFrom":makeQuery(id+"F11.opRevolve","SWEPT_FACE",FACE,{"disambiguationData":[OSD([subQ2])]})});Q9=makeQuery(id+"F19.boolean.opBoolean","SPLIT",FACE,{"disambiguationData":[TD([makeQuery(id+"F19.opPattern","COPY",FACE,{"derivedFrom":makeQuery(id+"F18.opExtrude","SWEPT_FACE",FACE,{"disambiguationData":[OSD([sQuery(id+"F17.wireOp",EDGE,"E70")])]}),"instanceName":"1"})])],"derivedFrom":makeQuery(id+"F15.boolean.opBoolean","SPLIT",FACE,{"disambiguationData":[TD([subQ1])],"derivedFrom":subQ3})});}
            var Q10;
            {var subQ2=sQuery(id+"F10.wireOp",EDGE,"E49.filletArc");var subQ3=makeQuery(id+"F11.boolean.opBoolean","COPY",FACE,{"derivedFrom":makeQuery(id+"F11.opRevolve","SWEPT_FACE",FACE,{"disambiguationData":[OSD([subQ2])]})});var subQ8=sQuery(id+"F13.wireOp",EDGE,"E55");var subQ9=makeQuery(id+"F14.opExtrude","SWEPT_FACE",FACE,{"disambiguationData":[OSD([subQ8])]});Q10=makeQuery(id+"F19.boolean.opBoolean","SPLIT",FACE,{"disambiguationData":[TD([makeQuery(id+"F18.opExtrude","SWEPT_FACE",FACE,{"disambiguationData":[OSD([sQuery(id+"F17.wireOp",EDGE,"E76.MirrorCS")])]})])],"derivedFrom":makeQuery(id+"F15.boolean.opBoolean","SPLIT",FACE,{"disambiguationData":[TD([subQ9])],"derivedFrom":subQ3})});}
            var Q11;
            {var subQ0=sQuery(id+"F13.wireOp",EDGE,"E58");var subQ1=makeQuery(id+"F14.opExtrude","SWEPT_FACE",FACE,{"disambiguationData":[OSD([subQ0])]});var subQ2=sQuery(id+"F10.wireOp",EDGE,"E42");var subQ3=makeQuery(id+"F11.boolean.opBoolean","COPY",FACE,{"derivedFrom":makeQuery(id+"F11.opRevolve","SWEPT_FACE",FACE,{"disambiguationData":[OSD([subQ2])]})});Q11=makeQuery(id+"F19.boolean.opBoolean","SPLIT",FACE,{"disambiguationData":[TD([makeQuery(id+"F18.opExtrude","SWEPT_FACE",FACE,{"disambiguationData":[OSD([sQuery(id+"F17.wireOp",EDGE,"E77.MirrorCS")])]})])],"derivedFrom":makeQuery(id+"F15.boolean.opBoolean","SPLIT",FACE,{"disambiguationData":[TD([subQ1])],"derivedFrom":subQ3})});}
            var Q12;
            {var subQ2=sQuery(id+"F10.wireOp",EDGE,"E49.filletArc");var subQ3=makeQuery(id+"F11.boolean.opBoolean","COPY",FACE,{"derivedFrom":makeQuery(id+"F11.opRevolve","SWEPT_FACE",FACE,{"disambiguationData":[OSD([subQ2])]})});Q12=makeQuery(id+"F19.boolean.opBoolean","SPLIT",FACE,{"disambiguationData":[TD([makeQuery(id+"F18.opExtrude","SWEPT_FACE",FACE,{"disambiguationData":[OSD([sQuery(id+"F17.wireOp",EDGE,"E74.filletArc")])]})])],"derivedFrom":makeQuery(id+"F15.boolean.opBoolean","SPLIT",FACE,{"disambiguationData":[TD([makeQuery(id+"F14.opExtrude","SWEPT_FACE",FACE,{"disambiguationData":[OSD([sQuery(id+"F13.wireOp",EDGE,"E55")])]})])],"derivedFrom":subQ3})});}
            var Q13;
            {var subQ4=sQuery(id+"F10.wireOp",EDGE,"E44");var subQ5=makeQuery(id+"F11.boolean.opBoolean","COPY",FACE,{"derivedFrom":makeQuery(id+"F11.opRevolve","SWEPT_FACE",FACE,{"disambiguationData":[OSD([subQ4])]})});Q13=makeQuery(id+"F19.boolean.opBoolean","SPLIT",FACE,{"disambiguationData":[TD([makeQuery(id+"F18.opExtrude","SWEPT_FACE",FACE,{"disambiguationData":[OSD([sQuery(id+"F17.wireOp",EDGE,"E70")])]})])],"derivedFrom":makeQuery(id+"F15.boolean.opBoolean","SPLIT",FACE,{"disambiguationData":[TD([makeQuery(id+"F14.opExtrude","SWEPT_FACE",FACE,{"disambiguationData":[OSD([sQuery(id+"F13.wireOp",EDGE,"E55")])]})])],"derivedFrom":subQ5})});}
            var Q14;
            {var subQ2=sQuery(id+"F10.wireOp",EDGE,"E42");var subQ3=makeQuery(id+"F11.boolean.opBoolean","COPY",FACE,{"derivedFrom":makeQuery(id+"F11.opRevolve","SWEPT_FACE",FACE,{"disambiguationData":[OSD([subQ2])]})});Q14=makeQuery(id+"F19.boolean.opBoolean","SPLIT",FACE,{"disambiguationData":[TD([makeQuery(id+"F18.opExtrude","SWEPT_FACE",FACE,{"disambiguationData":[OSD([sQuery(id+"F17.wireOp",EDGE,"E70")])]})])],"derivedFrom":makeQuery(id+"F15.boolean.opBoolean","SPLIT",FACE,{"disambiguationData":[TD([makeQuery(id+"F14.opExtrude","SWEPT_FACE",FACE,{"disambiguationData":[OSD([sQuery(id+"F13.wireOp",EDGE,"E58")])]})])],"derivedFrom":subQ3})});}
            var Q15;
            {var subQ0=sQuery(id+"F13.wireOp",EDGE,"E55");var subQ1=makeQuery(id+"F14.opExtrude","SWEPT_FACE",FACE,{"disambiguationData":[OSD([subQ0])]});var subQ2=sQuery(id+"F10.wireOp",EDGE,"E44");var subQ3=makeQuery(id+"F11.boolean.opBoolean","COPY",FACE,{"derivedFrom":makeQuery(id+"F11.opRevolve","SWEPT_FACE",FACE,{"disambiguationData":[OSD([subQ2])]})});Q15=makeQuery(id+"F19.boolean.opBoolean","SPLIT",FACE,{"disambiguationData":[TD([makeQuery(id+"F18.opExtrude","SWEPT_FACE",FACE,{"disambiguationData":[OSD([sQuery(id+"F17.wireOp",EDGE,"E77.MirrorCS")])]})])],"derivedFrom":makeQuery(id+"F15.boolean.opBoolean","SPLIT",FACE,{"disambiguationData":[TD([subQ1])],"derivedFrom":subQ3})});}
            var Q16;
            {var subQ2=sQuery(id+"F10.wireOp",EDGE,"E44");var subQ3=makeQuery(id+"F11.boolean.opBoolean","COPY",FACE,{"derivedFrom":makeQuery(id+"F11.opRevolve","SWEPT_FACE",FACE,{"disambiguationData":[OSD([subQ2])]})});Q16=makeQuery(id+"F19.boolean.opBoolean","SPLIT",FACE,{"disambiguationData":[TD([makeQuery(id+"F19.opPattern","COPY",FACE,{"derivedFrom":makeQuery(id+"F18.opExtrude","SWEPT_FACE",FACE,{"disambiguationData":[OSD([sQuery(id+"F17.wireOp",EDGE,"E77.MirrorCS")])]}),"instanceName":"1"})])],"derivedFrom":makeQuery(id+"F15.boolean.opBoolean","SPLIT",FACE,{"disambiguationData":[TD([makeQuery(id+"F14.opExtrude","SWEPT_FACE",FACE,{"disambiguationData":[OSD([sQuery(id+"F13.wireOp",EDGE,"E64.MirrorCS")])]})])],"derivedFrom":subQ3})});}
            var Q17;
            {var subQ2=sQuery(id+"F13.wireOp",EDGE,"E64.MirrorCS");var subQ3=makeQuery(id+"F15.opPattern","COPY",FACE,{"derivedFrom":makeQuery(id+"F14.opExtrude","SWEPT_FACE",FACE,{"disambiguationData":[OSD([subQ2])]}),"instanceName":"1"});var subQ4=sQuery(id+"F10.wireOp",EDGE,"E44");var subQ5=makeQuery(id+"F11.boolean.opBoolean","COPY",FACE,{"derivedFrom":makeQuery(id+"F11.opRevolve","SWEPT_FACE",FACE,{"disambiguationData":[OSD([subQ4])]})});Q17=makeQuery(id+"F19.boolean.opBoolean","SPLIT",FACE,{"disambiguationData":[TD([makeQuery(id+"F19.opPattern","COPY",FACE,{"derivedFrom":makeQuery(id+"F18.opExtrude","SWEPT_FACE",FACE,{"disambiguationData":[OSD([sQuery(id+"F17.wireOp",EDGE,"E70")])]}),"instanceName":"2"})])],"derivedFrom":makeQuery(id+"F15.boolean.opBoolean","SPLIT",FACE,{"disambiguationData":[TD([subQ3])],"derivedFrom":subQ5})});}
            var Q18;
            {var subQ0=sQuery(id+"F13.wireOp",EDGE,"E63.MirrorCS");var subQ1=makeQuery(id+"F15.opPattern","COPY",FACE,{"derivedFrom":makeQuery(id+"F14.opExtrude","SWEPT_FACE",FACE,{"disambiguationData":[OSD([subQ0])]}),"instanceName":"1"});var subQ2=sQuery(id+"F10.wireOp",EDGE,"E49.filletArc");var subQ3=makeQuery(id+"F11.boolean.opBoolean","COPY",FACE,{"derivedFrom":makeQuery(id+"F11.opRevolve","SWEPT_FACE",FACE,{"disambiguationData":[OSD([subQ2])]})});Q18=makeQuery(id+"F19.boolean.opBoolean","SPLIT",FACE,{"disambiguationData":[TD([makeQuery(id+"F19.opPattern","COPY",FACE,{"derivedFrom":makeQuery(id+"F18.opExtrude","SWEPT_FACE",FACE,{"disambiguationData":[OSD([sQuery(id+"F17.wireOp",EDGE,"E70")])]}),"instanceName":"2"})])],"derivedFrom":makeQuery(id+"F15.boolean.opBoolean","SPLIT",FACE,{"disambiguationData":[TD([subQ1])],"derivedFrom":subQ3})});}
            var Q19;
            {var subQ0=sQuery(id+"F13.wireOp",EDGE,"E65.MirrorCS");var subQ1=makeQuery(id+"F15.opPattern","COPY",FACE,{"derivedFrom":makeQuery(id+"F14.opExtrude","SWEPT_FACE",FACE,{"disambiguationData":[OSD([subQ0])]}),"instanceName":"1"});var subQ2=sQuery(id+"F10.wireOp",EDGE,"E42");var subQ3=makeQuery(id+"F11.boolean.opBoolean","COPY",FACE,{"derivedFrom":makeQuery(id+"F11.opRevolve","SWEPT_FACE",FACE,{"disambiguationData":[OSD([subQ2])]})});Q19=makeQuery(id+"F19.boolean.opBoolean","SPLIT",FACE,{"disambiguationData":[TD([makeQuery(id+"F19.opPattern","COPY",FACE,{"derivedFrom":makeQuery(id+"F18.opExtrude","SWEPT_FACE",FACE,{"disambiguationData":[OSD([sQuery(id+"F17.wireOp",EDGE,"E70")])]}),"instanceName":"2"})])],"derivedFrom":makeQuery(id+"F15.boolean.opBoolean","SPLIT",FACE,{"disambiguationData":[TD([subQ1])],"derivedFrom":subQ3})});}
            var Q20;
            {var subQ2=sQuery(id+"F10.wireOp",EDGE,"E42");var subQ3=makeQuery(id+"F11.boolean.opBoolean","COPY",FACE,{"derivedFrom":makeQuery(id+"F11.opRevolve","SWEPT_FACE",FACE,{"disambiguationData":[OSD([subQ2])]})});Q20=makeQuery(id+"F19.boolean.opBoolean","SPLIT",FACE,{"disambiguationData":[TD([makeQuery(id+"F19.opPattern","COPY",FACE,{"derivedFrom":makeQuery(id+"F18.opExtrude","SWEPT_FACE",FACE,{"disambiguationData":[OSD([sQuery(id+"F17.wireOp",EDGE,"E77.MirrorCS")])]}),"instanceName":"2"})])],"derivedFrom":makeQuery(id+"F15.boolean.opBoolean","SPLIT",FACE,{"disambiguationData":[TD([makeQuery(id+"F15.opPattern","COPY",FACE,{"derivedFrom":makeQuery(id+"F14.opExtrude","SWEPT_FACE",FACE,{"disambiguationData":[OSD([sQuery(id+"F13.wireOp",EDGE,"E65.MirrorCS")])]}),"instanceName":"1"})])],"derivedFrom":subQ3})});}
            var Q21;
            {var subQ4=sQuery(id+"F10.wireOp",EDGE,"E44");var subQ5=makeQuery(id+"F11.boolean.opBoolean","COPY",FACE,{"derivedFrom":makeQuery(id+"F11.opRevolve","SWEPT_FACE",FACE,{"disambiguationData":[OSD([subQ4])]})});Q21=makeQuery(id+"F19.boolean.opBoolean","SPLIT",FACE,{"disambiguationData":[TD([makeQuery(id+"F19.opPattern","COPY",FACE,{"derivedFrom":makeQuery(id+"F18.opExtrude","SWEPT_FACE",FACE,{"disambiguationData":[OSD([sQuery(id+"F17.wireOp",EDGE,"E77.MirrorCS")])]}),"instanceName":"2"})])],"derivedFrom":makeQuery(id+"F15.boolean.opBoolean","SPLIT",FACE,{"disambiguationData":[TD([makeQuery(id+"F15.opPattern","COPY",FACE,{"derivedFrom":makeQuery(id+"F14.opExtrude","SWEPT_FACE",FACE,{"disambiguationData":[OSD([sQuery(id+"F13.wireOp",EDGE,"E64.MirrorCS")])]}),"instanceName":"1"})])],"derivedFrom":subQ5})});}
            var Q22;
            {var subQ6=sQuery(id+"F10.wireOp",EDGE,"E49.filletArc");var subQ7=makeQuery(id+"F11.boolean.opBoolean","COPY",FACE,{"derivedFrom":makeQuery(id+"F11.opRevolve","SWEPT_FACE",FACE,{"disambiguationData":[OSD([subQ6])]})});Q22=makeQuery(id+"F19.boolean.opBoolean","SPLIT",FACE,{"disambiguationData":[TD([makeQuery(id+"F19.opPattern","COPY",FACE,{"derivedFrom":makeQuery(id+"F18.opExtrude","SWEPT_FACE",FACE,{"disambiguationData":[OSD([sQuery(id+"F17.wireOp",EDGE,"E76.MirrorCS")])]}),"instanceName":"2"})])],"derivedFrom":makeQuery(id+"F15.boolean.opBoolean","SPLIT",FACE,{"disambiguationData":[TD([makeQuery(id+"F15.opPattern","COPY",FACE,{"derivedFrom":makeQuery(id+"F14.opExtrude","SWEPT_FACE",FACE,{"disambiguationData":[OSD([sQuery(id+"F13.wireOp",EDGE,"E63.MirrorCS")])]}),"instanceName":"1"})])],"derivedFrom":subQ7})});}
            var Q23;
            {var subQ2=sQuery(id+"F10.wireOp",EDGE,"E44");var subQ3=makeQuery(id+"F11.boolean.opBoolean","COPY",FACE,{"derivedFrom":makeQuery(id+"F11.opRevolve","SWEPT_FACE",FACE,{"disambiguationData":[OSD([subQ2])]})});Q23=makeQuery(id+"F19.boolean.opBoolean","SPLIT",FACE,{"disambiguationData":[TD([makeQuery(id+"F19.opPattern","COPY",FACE,{"derivedFrom":makeQuery(id+"F18.opExtrude","SWEPT_FACE",FACE,{"disambiguationData":[OSD([sQuery(id+"F17.wireOp",EDGE,"E77.MirrorCS")])]}),"instanceName":"3"})])],"derivedFrom":makeQuery(id+"F15.boolean.opBoolean","SPLIT",FACE,{"disambiguationData":[TD([makeQuery(id+"F15.opPattern","COPY",FACE,{"derivedFrom":makeQuery(id+"F14.opExtrude","SWEPT_FACE",FACE,{"disambiguationData":[OSD([sQuery(id+"F13.wireOp",EDGE,"E64.MirrorCS")])]}),"instanceName":"2"})])],"derivedFrom":subQ3})});}
            var Q24;
            {var subQ0=sQuery(id+"F13.wireOp",EDGE,"E63.MirrorCS");var subQ1=makeQuery(id+"F15.opPattern","COPY",FACE,{"derivedFrom":makeQuery(id+"F14.opExtrude","SWEPT_FACE",FACE,{"disambiguationData":[OSD([subQ0])]}),"instanceName":"3"});var subQ2=sQuery(id+"F10.wireOp",EDGE,"E49.filletArc");var subQ3=makeQuery(id+"F11.boolean.opBoolean","COPY",FACE,{"derivedFrom":makeQuery(id+"F11.opRevolve","SWEPT_FACE",FACE,{"disambiguationData":[OSD([subQ2])]})});Q24=makeQuery(id+"F19.boolean.opBoolean","SPLIT",FACE,{"disambiguationData":[TD([makeQuery(id+"F19.opPattern","COPY",FACE,{"derivedFrom":makeQuery(id+"F18.opExtrude","SWEPT_FACE",FACE,{"disambiguationData":[OSD([sQuery(id+"F17.wireOp",EDGE,"E70")])]}),"instanceName":"4"})])],"derivedFrom":makeQuery(id+"F15.boolean.opBoolean","SPLIT",FACE,{"disambiguationData":[TD([subQ1])],"derivedFrom":subQ3})});}
            var Q25;
            {var subQ4=sQuery(id+"F10.wireOp",EDGE,"E44");var subQ5=makeQuery(id+"F11.boolean.opBoolean","COPY",FACE,{"derivedFrom":makeQuery(id+"F11.opRevolve","SWEPT_FACE",FACE,{"disambiguationData":[OSD([subQ4])]})});var subQ6=sQuery(id+"F13.wireOp",EDGE,"E64.MirrorCS");var subQ7=makeQuery(id+"F15.opPattern","COPY",FACE,{"derivedFrom":makeQuery(id+"F14.opExtrude","SWEPT_FACE",FACE,{"disambiguationData":[OSD([subQ6])]}),"instanceName":"3"});Q25=makeQuery(id+"F19.boolean.opBoolean","SPLIT",FACE,{"disambiguationData":[TD([makeQuery(id+"F19.opPattern","COPY",FACE,{"derivedFrom":makeQuery(id+"F18.opExtrude","SWEPT_FACE",FACE,{"disambiguationData":[OSD([sQuery(id+"F17.wireOp",EDGE,"E70")])]}),"instanceName":"4"})])],"derivedFrom":makeQuery(id+"F15.boolean.opBoolean","SPLIT",FACE,{"disambiguationData":[TD([subQ7])],"derivedFrom":subQ5})});}
            var Q26;
            {var subQ0=sQuery(id+"F13.wireOp",EDGE,"E65.MirrorCS");var subQ1=makeQuery(id+"F15.opPattern","COPY",FACE,{"derivedFrom":makeQuery(id+"F14.opExtrude","SWEPT_FACE",FACE,{"disambiguationData":[OSD([subQ0])]}),"instanceName":"3"});var subQ2=sQuery(id+"F10.wireOp",EDGE,"E42");var subQ3=makeQuery(id+"F11.boolean.opBoolean","COPY",FACE,{"derivedFrom":makeQuery(id+"F11.opRevolve","SWEPT_FACE",FACE,{"disambiguationData":[OSD([subQ2])]})});Q26=makeQuery(id+"F19.boolean.opBoolean","SPLIT",FACE,{"disambiguationData":[TD([makeQuery(id+"F19.opPattern","COPY",FACE,{"derivedFrom":makeQuery(id+"F18.opExtrude","SWEPT_FACE",FACE,{"disambiguationData":[OSD([sQuery(id+"F17.wireOp",EDGE,"E70")])]}),"instanceName":"4"})])],"derivedFrom":makeQuery(id+"F15.boolean.opBoolean","SPLIT",FACE,{"disambiguationData":[TD([subQ1])],"derivedFrom":subQ3})});}
            var Q27;
            {var subQ2=sQuery(id+"F10.wireOp",EDGE,"E42");var subQ3=makeQuery(id+"F11.boolean.opBoolean","COPY",FACE,{"derivedFrom":makeQuery(id+"F11.opRevolve","SWEPT_FACE",FACE,{"disambiguationData":[OSD([subQ2])]})});Q27=makeQuery(id+"F19.boolean.opBoolean","SPLIT",FACE,{"disambiguationData":[TD([makeQuery(id+"F19.opPattern","COPY",FACE,{"derivedFrom":makeQuery(id+"F18.opExtrude","SWEPT_FACE",FACE,{"disambiguationData":[OSD([sQuery(id+"F17.wireOp",EDGE,"E77.MirrorCS")])]}),"instanceName":"4"})])],"derivedFrom":makeQuery(id+"F15.boolean.opBoolean","SPLIT",FACE,{"disambiguationData":[TD([makeQuery(id+"F15.opPattern","COPY",FACE,{"derivedFrom":makeQuery(id+"F14.opExtrude","SWEPT_FACE",FACE,{"disambiguationData":[OSD([sQuery(id+"F13.wireOp",EDGE,"E65.MirrorCS")])]}),"instanceName":"3"})])],"derivedFrom":subQ3})});}
            var Q28;
            {var subQ4=sQuery(id+"F10.wireOp",EDGE,"E44");var subQ5=makeQuery(id+"F11.boolean.opBoolean","COPY",FACE,{"derivedFrom":makeQuery(id+"F11.opRevolve","SWEPT_FACE",FACE,{"disambiguationData":[OSD([subQ4])]})});Q28=makeQuery(id+"F19.boolean.opBoolean","SPLIT",FACE,{"disambiguationData":[TD([makeQuery(id+"F19.opPattern","COPY",FACE,{"derivedFrom":makeQuery(id+"F18.opExtrude","SWEPT_FACE",FACE,{"disambiguationData":[OSD([sQuery(id+"F17.wireOp",EDGE,"E77.MirrorCS")])]}),"instanceName":"4"})])],"derivedFrom":makeQuery(id+"F15.boolean.opBoolean","SPLIT",FACE,{"disambiguationData":[TD([makeQuery(id+"F15.opPattern","COPY",FACE,{"derivedFrom":makeQuery(id+"F14.opExtrude","SWEPT_FACE",FACE,{"disambiguationData":[OSD([sQuery(id+"F13.wireOp",EDGE,"E64.MirrorCS")])]}),"instanceName":"3"})])],"derivedFrom":subQ5})});}
            var Q29;
            {var subQ2=sQuery(id+"F10.wireOp",EDGE,"E49.filletArc");var subQ3=makeQuery(id+"F11.boolean.opBoolean","COPY",FACE,{"derivedFrom":makeQuery(id+"F11.opRevolve","SWEPT_FACE",FACE,{"disambiguationData":[OSD([subQ2])]})});Q29=makeQuery(id+"F19.boolean.opBoolean","SPLIT",FACE,{"disambiguationData":[TD([makeQuery(id+"F19.opPattern","COPY",FACE,{"derivedFrom":makeQuery(id+"F18.opExtrude","SWEPT_FACE",FACE,{"disambiguationData":[OSD([sQuery(id+"F17.wireOp",EDGE,"E76.MirrorCS")])]}),"instanceName":"4"})])],"derivedFrom":makeQuery(id+"F15.boolean.opBoolean","SPLIT",FACE,{"disambiguationData":[TD([makeQuery(id+"F15.opPattern","COPY",FACE,{"derivedFrom":makeQuery(id+"F14.opExtrude","SWEPT_FACE",FACE,{"disambiguationData":[OSD([sQuery(id+"F13.wireOp",EDGE,"E63.MirrorCS")])]}),"instanceName":"3"})])],"derivedFrom":subQ3})});}
            var Q30;
            {var subQ1=makeQuery(id+"F11.boolean.opBoolean","COPY",FACE,{"derivedFrom":makeQuery(id+"F11.opRevolve","SWEPT_FACE",FACE,{"disambiguationData":[OSD([sQuery(id+"F10.wireOp",EDGE,"E42")])]})});var subQ3=makeQuery(id+"F15.opPattern","COPY",FACE,{"derivedFrom":makeQuery(id+"F14.opExtrude","SWEPT_FACE",FACE,{"disambiguationData":[OSD([sQuery(id+"F13.wireOp",EDGE,"E65.MirrorCS")])]}),"instanceName":"4"});Q30=makeQuery(id+"F19.boolean.opBoolean","SPLIT",FACE,{"disambiguationData":[TD([makeQuery(id+"F19.opPattern","COPY",FACE,{"derivedFrom":makeQuery(id+"F18.opExtrude","SWEPT_FACE",FACE,{"disambiguationData":[OSD([sQuery(id+"F17.wireOp",EDGE,"E70")])]}),"instanceName":"5"})])],"derivedFrom":makeQuery(id+"F15.boolean.opBoolean","SPLIT",FACE,{"disambiguationData":[TD([subQ3])],"derivedFrom":subQ1})});}
            var Q31;
            {var subQ2=sQuery(id+"F13.wireOp",EDGE,"E63.MirrorCS");var subQ3=makeQuery(id+"F15.opPattern","COPY",FACE,{"derivedFrom":makeQuery(id+"F14.opExtrude","SWEPT_FACE",FACE,{"disambiguationData":[OSD([subQ2])]}),"instanceName":"4"});var subQ4=makeQuery(id+"F15.opPattern","COPY",FACE,{"derivedFrom":makeQuery(id+"F14.opExtrude","SWEPT_FACE",FACE,{"disambiguationData":[OSD([sQuery(id+"F13.wireOp",EDGE,"E64.MirrorCS")])]}),"instanceName":"4"});Q31=makeQuery(id+"F19.boolean.opBoolean","SPLIT",FACE,{"disambiguationData":[TD([makeQuery(id+"F15.boolean.opBoolean","COPY",FACE,{"derivedFrom":subQ4})])],"derivedFrom":makeQuery(id+"F15.boolean.opBoolean","SPLIT",FACE,{"disambiguationData":[TD([subQ3])],"derivedFrom":makeQuery(id+"F11.boolean.opBoolean","COPY",FACE,{"derivedFrom":makeQuery(id+"F11.opRevolve","SWEPT_FACE",FACE,{"disambiguationData":[OSD([sQuery(id+"F10.wireOp",EDGE,"E49.filletArc")])]})})})});}
            var Q32;
            {var subQ1=makeQuery(id+"F11.boolean.opBoolean","COPY",FACE,{"derivedFrom":makeQuery(id+"F11.opRevolve","SWEPT_FACE",FACE,{"disambiguationData":[OSD([sQuery(id+"F10.wireOp",EDGE,"E42")])]})});Q32=makeQuery(id+"F19.boolean.opBoolean","SPLIT",FACE,{"disambiguationData":[TD([makeQuery(id+"F19.opPattern","COPY",FACE,{"derivedFrom":makeQuery(id+"F18.opExtrude","SWEPT_FACE",FACE,{"disambiguationData":[OSD([sQuery(id+"F17.wireOp",EDGE,"E77.MirrorCS")])]}),"instanceName":"5"})])],"derivedFrom":makeQuery(id+"F15.boolean.opBoolean","SPLIT",FACE,{"disambiguationData":[TD([makeQuery(id+"F15.opPattern","COPY",FACE,{"derivedFrom":makeQuery(id+"F14.opExtrude","SWEPT_FACE",FACE,{"disambiguationData":[OSD([sQuery(id+"F13.wireOp",EDGE,"E65.MirrorCS")])]}),"instanceName":"4"})])],"derivedFrom":subQ1})});}
            var Q33;
            {var subQ4=makeQuery(id+"F15.opPattern","COPY",FACE,{"derivedFrom":makeQuery(id+"F14.opExtrude","SWEPT_FACE",FACE,{"disambiguationData":[OSD([sQuery(id+"F13.wireOp",EDGE,"E55")])]}),"instanceName":"5"});Q33=makeQuery(id+"F19.boolean.opBoolean","SPLIT",FACE,{"disambiguationData":[TD([makeQuery(id+"F15.boolean.opBoolean","COPY",FACE,{"derivedFrom":subQ4})])],"derivedFrom":makeQuery(id+"F15.boolean.opBoolean","SPLIT",FACE,{"disambiguationData":[TD([makeQuery(id+"F15.opPattern","COPY",FACE,{"derivedFrom":makeQuery(id+"F14.opExtrude","SWEPT_FACE",FACE,{"disambiguationData":[OSD([sQuery(id+"F13.wireOp",EDGE,"E63.MirrorCS")])]}),"instanceName":"4"})])],"derivedFrom":makeQuery(id+"F11.boolean.opBoolean","COPY",FACE,{"derivedFrom":makeQuery(id+"F11.opRevolve","SWEPT_FACE",FACE,{"disambiguationData":[OSD([sQuery(id+"F10.wireOp",EDGE,"E49.filletArc")])]})})})});}
            var Q34;
            {var subQ4=sQuery(id+"F10.wireOp",EDGE,"E44");var subQ5=makeQuery(id+"F11.boolean.opBoolean","COPY",FACE,{"derivedFrom":makeQuery(id+"F11.opRevolve","SWEPT_FACE",FACE,{"disambiguationData":[OSD([subQ4])]})});Q34=makeQuery(id+"F19.boolean.opBoolean","SPLIT",FACE,{"disambiguationData":[TD([makeQuery(id+"F19.opPattern","COPY",FACE,{"derivedFrom":makeQuery(id+"F18.opExtrude","SWEPT_FACE",FACE,{"disambiguationData":[OSD([sQuery(id+"F17.wireOp",EDGE,"E77.MirrorCS")])]}),"instanceName":"5"})])],"derivedFrom":makeQuery(id+"F15.boolean.opBoolean","SPLIT",FACE,{"disambiguationData":[TD([makeQuery(id+"F15.opPattern","COPY",FACE,{"derivedFrom":makeQuery(id+"F14.opExtrude","SWEPT_FACE",FACE,{"disambiguationData":[OSD([sQuery(id+"F13.wireOp",EDGE,"E64.MirrorCS")])]}),"instanceName":"4"})])],"derivedFrom":subQ5})});}
            var Q35;
            {var subQ0=sQuery(id+"F13.wireOp",EDGE,"E64.MirrorCS");var subQ1=makeQuery(id+"F15.opPattern","COPY",FACE,{"derivedFrom":makeQuery(id+"F14.opExtrude","SWEPT_FACE",FACE,{"disambiguationData":[OSD([subQ0])]}),"instanceName":"4"});var subQ2=sQuery(id+"F10.wireOp",EDGE,"E44");var subQ3=makeQuery(id+"F11.boolean.opBoolean","COPY",FACE,{"derivedFrom":makeQuery(id+"F11.opRevolve","SWEPT_FACE",FACE,{"disambiguationData":[OSD([subQ2])]})});Q35=makeQuery(id+"F19.boolean.opBoolean","SPLIT",FACE,{"disambiguationData":[TD([makeQuery(id+"F19.opPattern","COPY",FACE,{"derivedFrom":makeQuery(id+"F18.opExtrude","SWEPT_FACE",FACE,{"disambiguationData":[OSD([sQuery(id+"F17.wireOp",EDGE,"E70")])]}),"instanceName":"5"})])],"derivedFrom":makeQuery(id+"F15.boolean.opBoolean","SPLIT",FACE,{"disambiguationData":[TD([subQ1])],"derivedFrom":subQ3})});}
            var Q36;
            {var subQ0=makeQuery(id+"F18.opExtrude","SWEPT_FACE",FACE,{"disambiguationData":[OSD([sQuery(id+"F17.wireOp",EDGE,"E72"),sQuery(id+"F17.wireOp",EDGE,"E79.MirrorCS")])]});var subQ1=makeQuery(id+"F14.opExtrude","SWEPT_FACE",FACE,{"disambiguationData":[OSD([sQuery(id+"F13.wireOp",EDGE,"E57"),sQuery(id+"F13.wireOp",EDGE,"E66.MirrorCS")])]});Q36=makeQuery(id+"F19.boolean.opBoolean","MERGE",FACE,{"derivedFrom":[makeQuery(id+"F15.boolean.opBoolean","MERGE",FACE,{"derivedFrom":[makeQuery(id+"F11.boolean.opBoolean","COPY",FACE,{"derivedFrom":makeQuery(id+"F11.opRevolve","SWEPT_FACE",FACE,{"disambiguationData":[OSD([sQuery(id+"F10.wireOp",EDGE,"E41")])]})}),subQ1,makeQuery(id+"F15.opPattern","COPY",FACE,{"derivedFrom":subQ1,"instanceName":"1"}),makeQuery(id+"F15.opPattern","COPY",FACE,{"derivedFrom":subQ1,"instanceName":"2"}),makeQuery(id+"F15.opPattern","COPY",FACE,{"derivedFrom":subQ1,"instanceName":"3"}),makeQuery(id+"F15.opPattern","COPY",FACE,{"derivedFrom":subQ1,"instanceName":"4"}),makeQuery(id+"F15.opPattern","COPY",FACE,{"derivedFrom":subQ1,"instanceName":"5"})]}),subQ0,makeQuery(id+"F19.opPattern","COPY",FACE,{"derivedFrom":subQ0,"instanceName":"1"}),makeQuery(id+"F19.opPattern","COPY",FACE,{"derivedFrom":subQ0,"instanceName":"2"}),makeQuery(id+"F19.opPattern","COPY",FACE,{"derivedFrom":subQ0,"instanceName":"3"}),makeQuery(id+"F19.opPattern","COPY",FACE,{"derivedFrom":subQ0,"instanceName":"4"}),makeQuery(id+"F19.opPattern","COPY",FACE,{"derivedFrom":subQ0,"instanceName":"5"})]});}
            var Q37;
            Q37=makeQuery(id+"F11.boolean.opBoolean","COPY",FACE,{"derivedFrom":makeQuery(id+"F11.opRevolve","SWEPT_FACE",FACE,{"disambiguationData":[OSD([sQuery(id+"F10.wireOp",EDGE,"E50")])]})});
            fillet(context, id + "F20", {"entities" : qUnion([Q0, Q1, Q2, Q3, Q4, Q5, Q6, Q7, Q8, Q9, Q10, Q11, Q12, Q13, Q14, Q15, Q16, Q17, Q18, Q19, Q20, Q21, Q22, Q23, Q24, Q25, Q26, Q27, Q28, Q29, Q30, Q31, Q32, Q33, Q34, Q35, Q36, Q37]), "radius" : 1.37 * mm, "tangentPropagation" : true, "allowEdgeOverflow" : false});
        }
        {
            var Q0;
            Q0=qCreatedBy(makeId("Front.planeOp"),FACE);
            var sketch = newSketch(context, id + "F21", { "sketchPlane" : qUnion([Q0])});
            skLineSegment(sketch, "E80", {"start": v(3, 16.87) * mm, "end": v(25.86, 16.87) * mm});
            skLineSegment(sketch, "E81", {"start": v(26.48, 14.7) * mm, "end": v(15.7, 7.98) * mm});
            skPoint(sketch, "E81.endSnap0", {"position": v(0.5, 16.87) * mm});
            skPoint(sketch, "E82.visualSharp", {"position": v(29.94, 16.87) * mm});
            skArc(sketch, "E82.filletArc", {"start": v(26.48, 14.7) * mm, "mid": v(26.98, 16.02) * mm, "end": v(25.86, 16.87) * mm});
            skPoint(sketch, "E83.orphan", {"position": v(7.96, 7.98) * mm});
            skLineSegment(sketch, "E84", {"start": v(15.7, 7.98) * mm, "end": v(7.96, 7.98) * mm});
            skLineSegment(sketch, "E85", {"start": v(7.96, 7.98) * mm, "end": v(2.1, 14.95) * mm});
            skArc(sketch, "E86.filletArc", {"start": v(3, 16.87) * mm, "mid": v(1.94, 16.2) * mm, "end": v(2.1, 14.95) * mm});
            skSolve(sketch);
        }
        {
            var Q0;
            Q0 = qSketchRegion(id + "F21", true);
            var Q1;
            Q1=sQuery(id+"F10.wireOp",EDGE,"E46");
            revolve(context, id + "F22", {"operationType" : NewBodyOperationType.REMOVE, "entities" : qUnion([Q0]), "axis" : qUnion([Q1]), "revolveType" : RevolveType.FULL, "oppositeDirection" : true});
        }
    });
